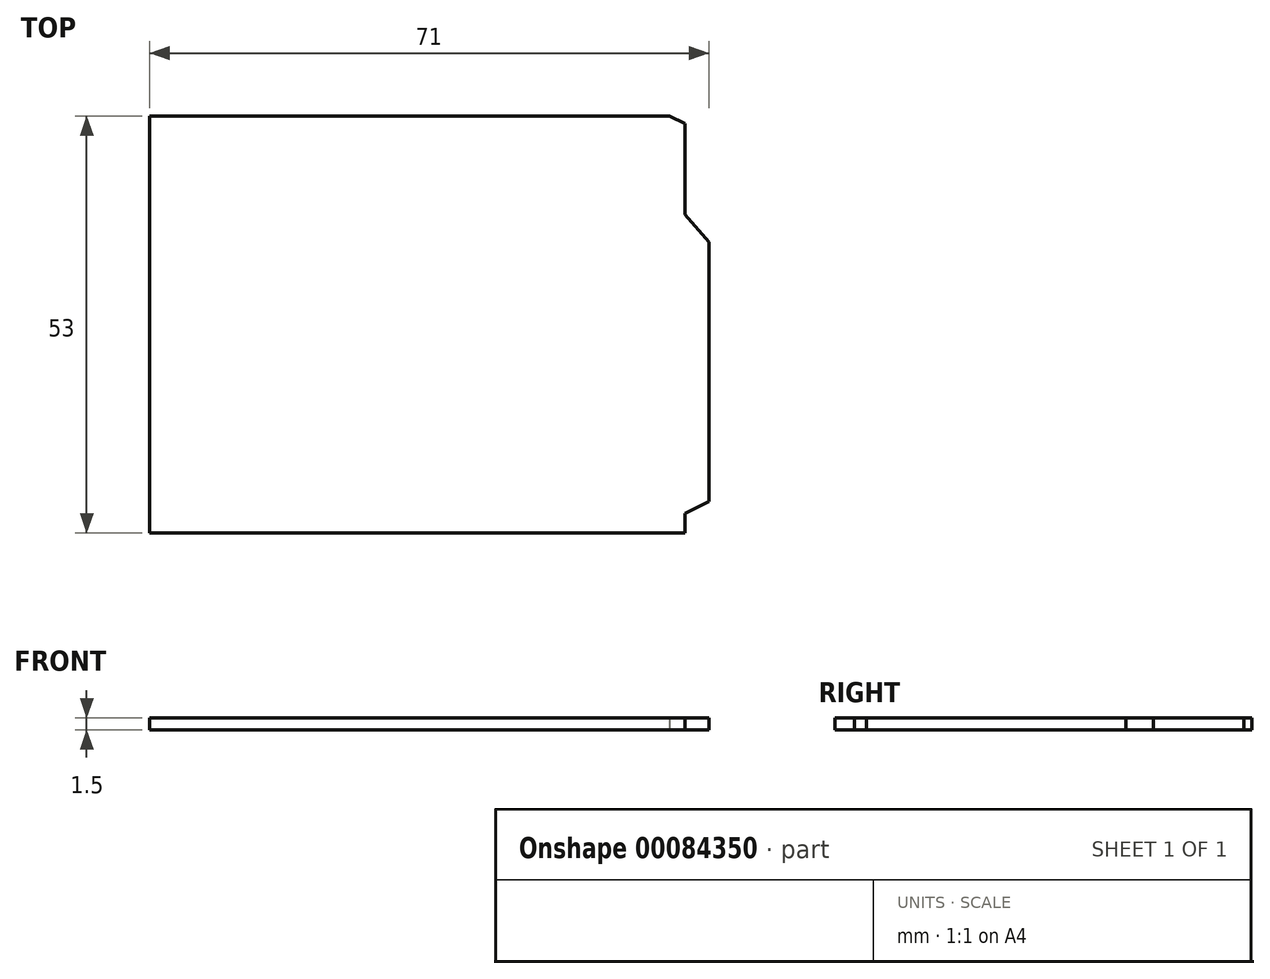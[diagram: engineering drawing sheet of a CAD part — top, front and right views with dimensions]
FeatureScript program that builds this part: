
annotation { "Feature Type Name" : "Feature", "Feature Type Description" : "" }
export const myFeature = defineFeature(function(context is Context, id is Id, definition is map)
    precondition{}
    {
        {
            var Q0;
            Q0=qCreatedBy(makeId("Top.planeOp"),FACE);
            var sketch = newSketch(context, id + "F0", { "sketchPlane" : qUnion([Q0])});
            skLineSegment(sketch, "E0.bottom", {"start": v(0, 0) * mm, "end": v(68, 0) * mm});
            skLineSegment(sketch, "E0.top", {"start": v(0, 53) * mm, "end": v(66, 53) * mm});
            skLineSegment(sketch, "E0.left", {"start": v(0, 0) * mm, "end": v(0, 53) * mm});
            skLineSegment(sketch, "E0.right", {"start": v(68, 0) * mm, "end": v(68, 52) * mm});
            skPoint(sketch, "E1", {"position": v(68, 37) * mm});
            skPoint(sketch, "E2", {"position": v(68, 40.5) * mm});
            skLineSegment(sketch, "E3", {"start": v(68, 37) * mm, "end": v(71, 37) * mm});
            skLineSegment(sketch, "E4", {"start": v(68, 40.5) * mm, "end": v(71, 37) * mm});
            skLineSegment(sketch, "E5", {"start": v(71, 37) * mm, "end": v(71, 4) * mm});
            skPoint(sketch, "E6", {"position": v(68, 2.5) * mm});
            skLineSegment(sketch, "E7", {"start": v(68, 2.5) * mm, "end": v(71, 4) * mm});
            skLineSegment(sketch, "E8", {"start": v(66, 53) * mm, "end": v(68, 52) * mm});
            skPoint(sketch, "E9.orphan", {"position": v(68, 53) * mm});
            skSolve(sketch);
        }
        {
            var Q0;
            Q0 = qSketchRegion(id + "F0", true);
            extrude(context, id + "F1", {"entities" : qUnion([Q0]), "depth" : 1.5 * mm});
        }
    });
